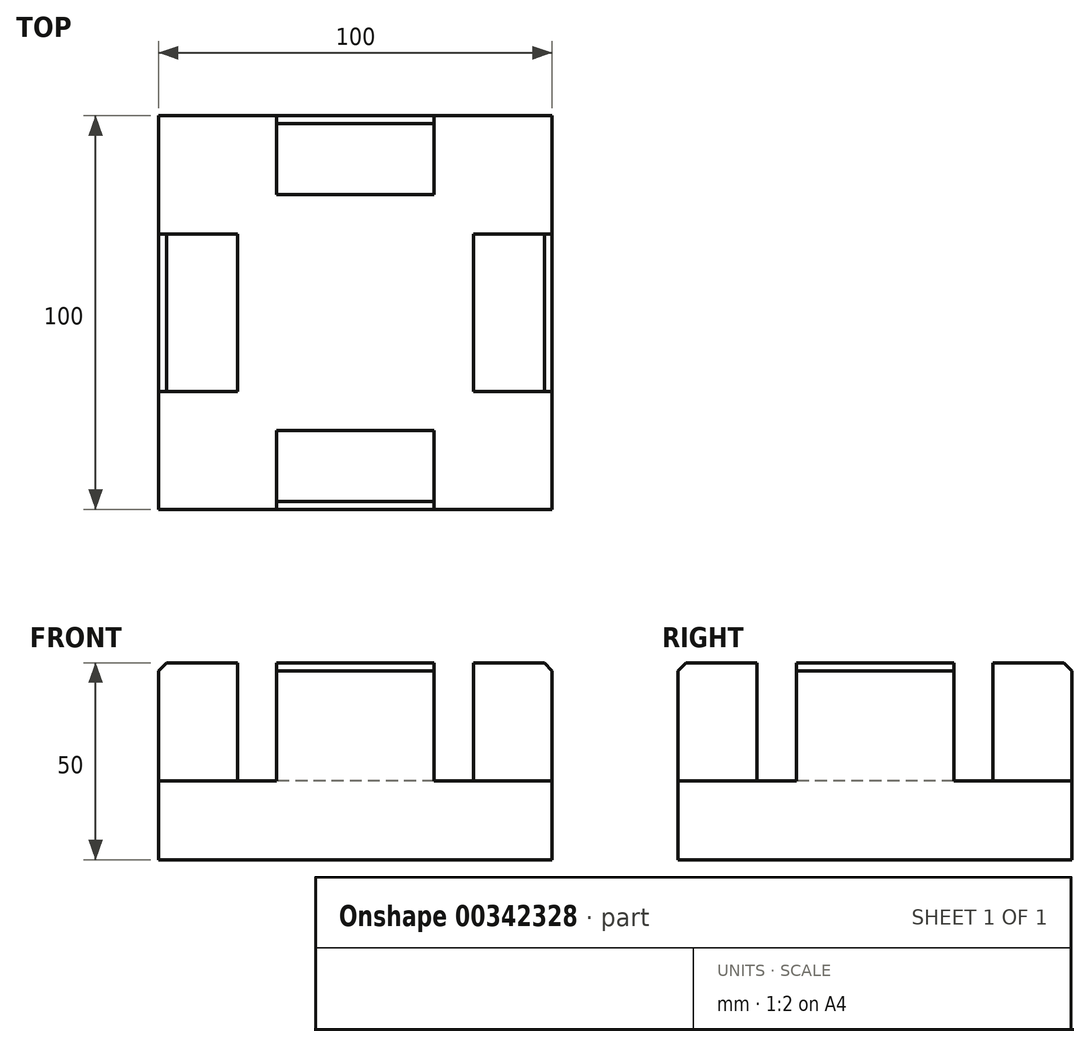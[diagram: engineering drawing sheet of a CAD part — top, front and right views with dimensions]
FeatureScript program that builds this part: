
annotation { "Feature Type Name" : "Feature", "Feature Type Description" : "" }
export const myFeature = defineFeature(function(context is Context, id is Id, definition is map)
    precondition{}
    {
        {
            var Q0;
            Q0=qCreatedBy(makeId("Top.planeOp"),FACE);
            var sketch = newSketch(context, id + "F0", { "sketchPlane" : qUnion([Q0])});
            skLineSegment(sketch, "E0.bottom", {"start": v(50, 50) * mm, "end": v(-50, 50) * mm});
            skLineSegment(sketch, "E0.top", {"start": v(50, -50) * mm, "end": v(-50, -50) * mm});
            skLineSegment(sketch, "E0.left", {"start": v(50, 50) * mm, "end": v(50, -50) * mm});
            skLineSegment(sketch, "E0.right", {"start": v(-50, 50) * mm, "end": v(-50, -50) * mm});
            skPoint(sketch, "E0.middle", {"position": v(0, 0) * mm});
            skSolve(sketch);
        }
        {
            var Q0;
            Q0=makeQuery(id+"F0.imprint","IMPRINT",FACE,{"disambiguationData":[TD([[makeQuery(id+"F0.imprint","IMPRINT",EDGE,{"derivedFrom":sQuery(id+"F0.wireOp",EDGE,"E0.bottom")}),1.0]])]});
            extrude(context, id + "F1", {"entities" : qUnion([Q0]), "depth" : 50 * mm});
        }
        {
            var Q0;
            Q0=makeQuery(id+"F1.opExtrude","CAP_FACE",FACE,{"disambiguationData":[OSD([sQuery(id+"F0.wireOp",EDGE,"E0.bottom"),sQuery(id+"F0.wireOp",EDGE,"E0.top"),sQuery(id+"F0.wireOp",EDGE,"E0.left"),sQuery(id+"F0.wireOp",EDGE,"E0.right")])],"isStart":false});
            var sketch = newSketch(context, id + "F2", { "sketchPlane" : qUnion([Q0])});
            skLineSegment(sketch, "E1.bottom", {"start": v(30, 30) * mm, "end": v(-30, 30) * mm});
            skLineSegment(sketch, "E1.top", {"start": v(30, -30) * mm, "end": v(-30, -30) * mm});
            skLineSegment(sketch, "E1.left", {"start": v(30, 30) * mm, "end": v(30, -30) * mm});
            skLineSegment(sketch, "E1.right", {"start": v(-30, 30) * mm, "end": v(-30, -30) * mm});
            skPoint(sketch, "E1.middle", {"position": v(0, 0) * mm});
            skSolve(sketch);
        }
        {
            var Q0;
            Q0=makeQuery(id+"F2.imprint","IMPRINT",FACE,{"disambiguationData":[TD([[makeQuery(id+"F2.imprint","IMPRINT",EDGE,{"derivedFrom":sQuery(id+"F2.wireOp",EDGE,"E1.bottom")}),1.0]])]});
            extrude(context, id + "F3", {"entities" : qUnion([Q0]), "operationType" : NewBodyOperationType.REMOVE, "oppositeDirection" : true, "depth" : 30 * mm});
        }
        {
            var Q0;
            Q0=makeQuery(id+"F1.opExtrude","CAP_FACE",FACE,{"disambiguationData":[OSD([sQuery(id+"F0.wireOp",EDGE,"E0.bottom"),sQuery(id+"F0.wireOp",EDGE,"E0.top"),sQuery(id+"F0.wireOp",EDGE,"E0.left"),sQuery(id+"F0.wireOp",EDGE,"E0.right")])],"isStart":false});
            var sketch = newSketch(context, id + "F4", { "sketchPlane" : qUnion([Q0])});
            skLineSegment(sketch, "E2.bottom", {"start": v(-50, 20) * mm, "end": v(-20, 20) * mm});
            skLineSegment(sketch, "E2.top", {"start": v(-50, 50) * mm, "end": v(-20, 50) * mm});
            skLineSegment(sketch, "E2.left", {"start": v(-50, 20) * mm, "end": v(-50, 50) * mm});
            skLineSegment(sketch, "E2.right", {"start": v(-20, 20) * mm, "end": v(-20, 50) * mm});
            skLineSegment(sketch, "E3.bottom", {"start": v(-50, -50) * mm, "end": v(-20, -50) * mm});
            skLineSegment(sketch, "E3.top", {"start": v(-50, -20) * mm, "end": v(-20, -20) * mm});
            skLineSegment(sketch, "E3.left", {"start": v(-50, -50) * mm, "end": v(-50, -20) * mm});
            skLineSegment(sketch, "E3.right", {"start": v(-20, -50) * mm, "end": v(-20, -20) * mm});
            skLineSegment(sketch, "E4.bottom", {"start": v(50, -50) * mm, "end": v(20, -50) * mm});
            skLineSegment(sketch, "E4.top", {"start": v(50, -20) * mm, "end": v(20, -20) * mm});
            skLineSegment(sketch, "E4.left", {"start": v(50, -50) * mm, "end": v(50, -20) * mm});
            skLineSegment(sketch, "E4.right", {"start": v(20, -50) * mm, "end": v(20, -20) * mm});
            skLineSegment(sketch, "E5.bottom", {"start": v(50, 50) * mm, "end": v(20, 50) * mm});
            skLineSegment(sketch, "E5.top", {"start": v(50, 20) * mm, "end": v(20, 20) * mm});
            skLineSegment(sketch, "E5.left", {"start": v(50, 50) * mm, "end": v(50, 20) * mm});
            skLineSegment(sketch, "E5.right", {"start": v(20, 50) * mm, "end": v(20, 20) * mm});
            skSolve(sketch);
        }
        {
            var Q0;
            {var subQ0=sQuery(id+"F4.wireOp",EDGE,"E2.right");var subQ1=sQuery(id+"F4.wireOp",EDGE,"E2.bottom");var subQ2=makeQuery(id+"F4.imprint","INTERSECT",VERTEX,{"derivedFrom":[subQ1,subQ0]});Q0=makeQuery(id+"F4.imprint","IMPRINT",FACE,{"disambiguationData":[TD([[makeQuery(id+"F4.imprint","IMPRINT",EDGE,{"disambiguationData":[TD([[subQ2,1.0]])],"derivedFrom":subQ1}),1.0]])]});}
            var Q1;
            {var subQ0=sQuery(id+"F4.wireOp",EDGE,"E3.right");var subQ1=sQuery(id+"F4.wireOp",EDGE,"E3.top");var subQ2=makeQuery(id+"F4.imprint","INTERSECT",VERTEX,{"derivedFrom":[subQ1,subQ0]});Q1=makeQuery(id+"F4.imprint","IMPRINT",FACE,{"disambiguationData":[TD([[makeQuery(id+"F4.imprint","IMPRINT",EDGE,{"disambiguationData":[TD([[subQ2,1.0]])],"derivedFrom":subQ1}),-1.0]])]});}
            var Q2;
            {var subQ0=sQuery(id+"F4.wireOp",EDGE,"E4.right");var subQ1=sQuery(id+"F4.wireOp",EDGE,"E4.top");var subQ2=makeQuery(id+"F4.imprint","INTERSECT",VERTEX,{"derivedFrom":[subQ1,subQ0]});Q2=makeQuery(id+"F4.imprint","IMPRINT",FACE,{"disambiguationData":[TD([[makeQuery(id+"F4.imprint","IMPRINT",EDGE,{"disambiguationData":[TD([[subQ2,1.0]])],"derivedFrom":subQ1}),1.0]])]});}
            var Q3;
            {var subQ0=sQuery(id+"F4.wireOp",EDGE,"E5.right");var subQ1=sQuery(id+"F4.wireOp",EDGE,"E5.top");var subQ2=makeQuery(id+"F4.imprint","INTERSECT",VERTEX,{"derivedFrom":[subQ1,subQ0]});Q3=makeQuery(id+"F4.imprint","IMPRINT",FACE,{"disambiguationData":[TD([[makeQuery(id+"F4.imprint","IMPRINT",EDGE,{"disambiguationData":[TD([[subQ2,1.0]])],"derivedFrom":subQ1}),-1.0]])]});}
            var Q4;
            {var subQ1=sQuery(id+"F4.wireOp",EDGE,"E2.top");Q4=makeQuery(id+"F4.imprint","IMPRINT",FACE,{"disambiguationData":[TD([[makeQuery(id+"F4.imprint","IMPRINT",EDGE,{"derivedFrom":subQ1}),1.0]])]});}
            var Q5;
            {var subQ1=sQuery(id+"F4.wireOp",EDGE,"E4.bottom");Q5=makeQuery(id+"F4.imprint","IMPRINT",FACE,{"disambiguationData":[TD([[makeQuery(id+"F4.imprint","IMPRINT",EDGE,{"derivedFrom":subQ1}),-1.0]])]});}
            var Q6;
            {var subQ1=sQuery(id+"F4.wireOp",EDGE,"E5.bottom");Q6=makeQuery(id+"F4.imprint","IMPRINT",FACE,{"disambiguationData":[TD([[makeQuery(id+"F4.imprint","IMPRINT",EDGE,{"derivedFrom":subQ1}),1.0]])]});}
            var Q7;
            {var subQ1=sQuery(id+"F4.wireOp",EDGE,"E3.bottom");Q7=makeQuery(id+"F4.imprint","IMPRINT",FACE,{"disambiguationData":[TD([[makeQuery(id+"F4.imprint","IMPRINT",EDGE,{"derivedFrom":subQ1}),-1.0]])]});}
            extrude(context, id + "F5", {"entities" : qUnion([Q0, Q1, Q2, Q3, Q4, Q5, Q6, Q7]), "operationType" : NewBodyOperationType.REMOVE, "oppositeDirection" : true, "depth" : 30 * mm});
        }
        {
            var Q0;
            Q0=makeQuery(id+"F1.opExtrude","CAP_EDGE",EDGE,{"disambiguationData":[OSD([sQuery(id+"F0.wireOp",EDGE,"E0.top")])],"isStart":false});
            var Q1;
            Q1=makeQuery(id+"F1.opExtrude","CAP_EDGE",EDGE,{"disambiguationData":[OSD([sQuery(id+"F0.wireOp",EDGE,"E0.left")])],"isStart":false});
            var Q2;
            Q2=makeQuery(id+"F1.opExtrude","CAP_EDGE",EDGE,{"disambiguationData":[OSD([sQuery(id+"F0.wireOp",EDGE,"E0.bottom")])],"isStart":false});
            var Q3;
            Q3=makeQuery(id+"F1.opExtrude","CAP_EDGE",EDGE,{"disambiguationData":[OSD([sQuery(id+"F0.wireOp",EDGE,"E0.right")])],"isStart":false});
            chamfer(context, id + "F6", {"entities" : qUnion([Q0, Q1, Q2, Q3]), "width" : 2 * mm, "tangentPropagation" : true});
        }
    });
